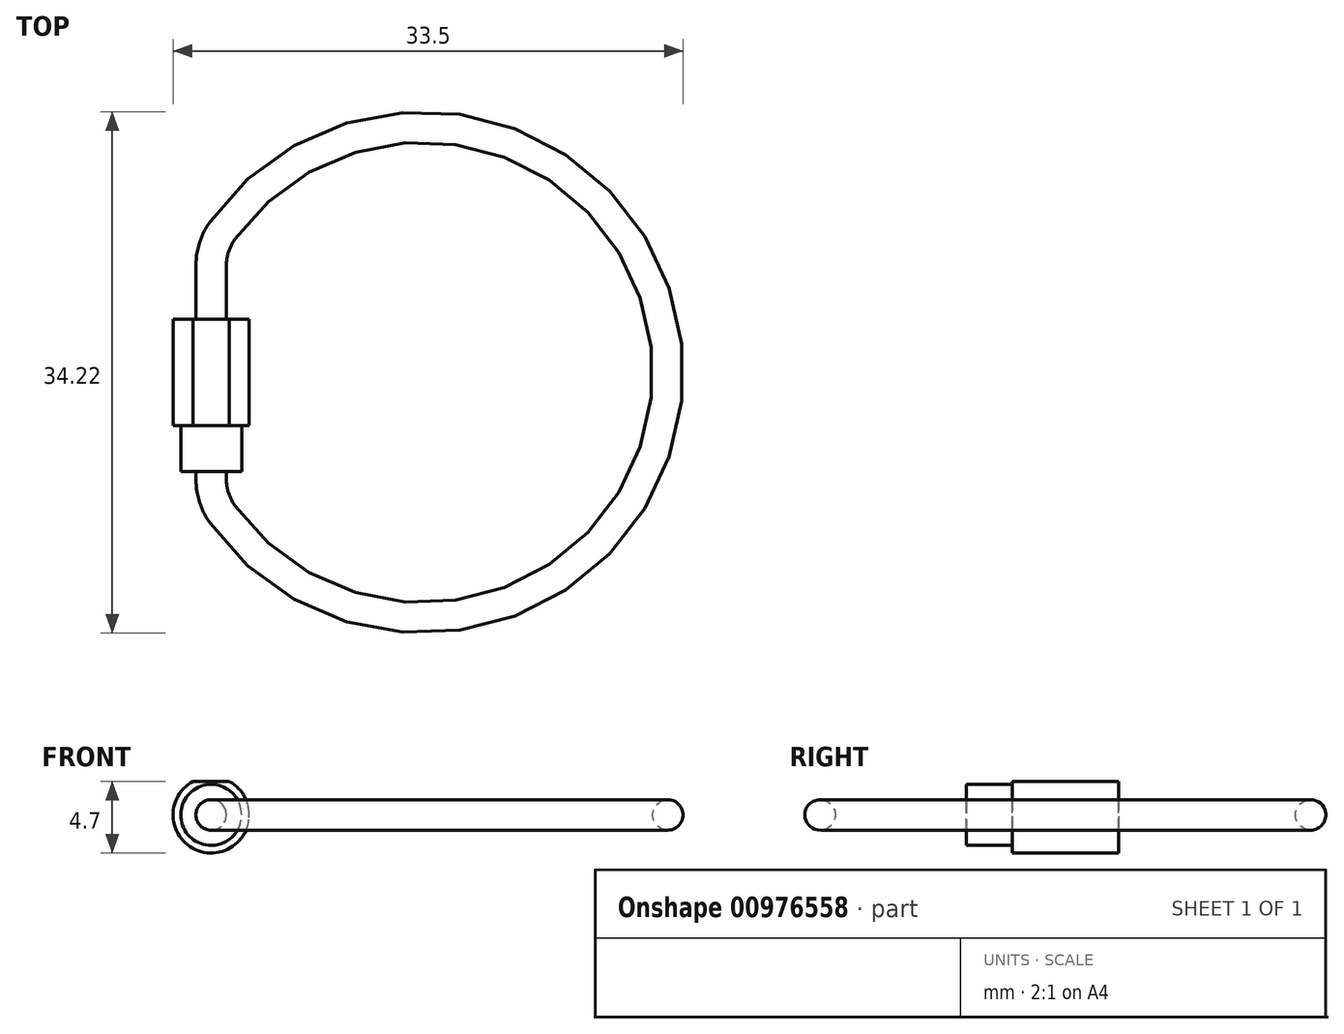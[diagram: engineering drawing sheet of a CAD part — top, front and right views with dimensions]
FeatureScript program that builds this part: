
annotation { "Feature Type Name" : "Feature", "Feature Type Description" : "" }
export const myFeature = defineFeature(function(context is Context, id is Id, definition is map)
    precondition{}
    {
        {
            var Q0;
            Q0=qCreatedBy(makeId("Front.planeOp"),FACE);
            var sketch = newSketch(context, id + "F0", { "sketchPlane" : qUnion([Q0])});
            skCircle(sketch, "E0", {"center": v(0, 0) * mm, "radius": 2.5 * mm});
            skSolve(sketch);
        }
        {
            var Q0;
            Q0=makeQuery(id+"F0.imprint","IMPRINT",FACE,{"disambiguationData":[TD([[makeQuery(id+"F0.imprint","IMPRINT",EDGE,{"derivedFrom":sQuery(id+"F0.wireOp",EDGE,"E0")}),1.0]])]});
            extrude(context, id + "F1", {"entities" : qUnion([Q0]), "endBound" : BoundingType.SYMMETRIC, "depth" : 7 * mm, "offsetDistance" : 25 * mm});
        }
        {
            var Q0;
            Q0=makeQuery(id+"F1.opExtrude","CAP_FACE",FACE,{"disambiguationData":[OSD([sQuery(id+"F0.wireOp",EDGE,"E0")])],"isStart":false});
            var sketch = newSketch(context, id + "F2", { "sketchPlane" : qUnion([Q0])});
            skLineSegment(sketch, "E1.bottom", {"start": v(-1.19, 2.5) * mm, "end": v(1.19, 2.5) * mm});
            skLineSegment(sketch, "E1.top", {"start": v(-1.19, 2.2) * mm, "end": v(1.19, 2.2) * mm});
            skLineSegment(sketch, "E1.left", {"start": v(-1.19, 2.5) * mm, "end": v(-1.19, 2.2) * mm});
            skLineSegment(sketch, "E1.right", {"start": v(1.19, 2.5) * mm, "end": v(1.19, 2.2) * mm});
            skSolve(sketch);
        }
        {
            var Q0;
            Q0 = qSketchRegion(id + "F2", true);
            extrude(context, id + "F3", {"entities" : qUnion([Q0]), "operationType" : NewBodyOperationType.REMOVE, "endBound" : BoundingType.THROUGH_ALL, "oppositeDirection" : true, "depth" : 25 * mm, "offsetDistance" : 25 * mm});
        }
        {
            var Q0;
            Q0=makeQuery(id+"F1.opExtrude","CAP_FACE",FACE,{"disambiguationData":[OSD([sQuery(id+"F0.wireOp",EDGE,"E0")])],"isStart":false});
            var sketch = newSketch(context, id + "F4", { "sketchPlane" : qUnion([Q0])});
            skCircle(sketch, "E2", {"center": v(0, 0) * mm, "radius": 2 * mm});
            skSolve(sketch);
        }
        {
            var Q0;
            Q0=makeQuery(id+"F4.imprint","IMPRINT",FACE,{"disambiguationData":[TD([[makeQuery(id+"F4.imprint","IMPRINT",EDGE,{"derivedFrom":sQuery(id+"F4.wireOp",EDGE,"E2")}),1.0]])]});
            extrude(context, id + "F5", {"entities" : qUnion([Q0]), "operationType" : NewBodyOperationType.ADD, "depth" : 3 * mm, "offsetDistance" : 25 * mm});
        }
        {
            var Q0;
            Q0=qCreatedBy(makeId("Top.planeOp"),FACE);
            var sketch = newSketch(context, id + "F6", { "sketchPlane" : qUnion([Q0])});
            skLineSegment(sketch, "E3", {"start": v(0, 0) * mm, "end": v(13.89, 0) * mm, "construction": true});
            skLineSegment(sketch, "E4", {"start": v(0, 7) * mm, "end": v(0, -7) * mm});
            skArc(sketch, "E5", {"start": v(0.74, 9.31) * mm, "mid": v(0.19, 8.21) * mm, "end": v(0, 7) * mm});
            skArc(sketch, "E6", {"start": v(0, -7) * mm, "mid": v(0.19, -8.21) * mm, "end": v(0.74, -9.31) * mm});
            skArc(sketch, "E7", {"start": v(0.74, -9.31) * mm, "mid": v(30, 0) * mm, "end": v(0.74, 9.31) * mm});
            skSolve(sketch);
        }
        {
            var Q0;
            Q0=makeQuery(id+"F5.opExtrude","CAP_FACE",FACE,{"disambiguationData":[OSD([sQuery(id+"F4.wireOp",EDGE,"E2")])],"isStart":false});
            var sketch = newSketch(context, id + "F7", { "sketchPlane" : qUnion([Q0])});
            skCircle(sketch, "E8", {"center": v(0, 0) * mm, "radius": 1 * mm});
            skSolve(sketch);
        }
        {
            var Q0;
            Q0=makeQuery(id+"F7.imprint","IMPRINT",FACE,{"disambiguationData":[TD([[makeQuery(id+"F7.imprint","IMPRINT",EDGE,{"derivedFrom":sQuery(id+"F7.wireOp",EDGE,"E8")}),1.0]])]});
            var Q1;
            Q1=sQuery(id+"F6.wireOp",EDGE,"E4");
            var Q2;
            Q2=sQuery(id+"F6.wireOp",EDGE,"E5");
            var Q3;
            Q3=sQuery(id+"F6.wireOp",EDGE,"E7");
            var Q4;
            Q4=sQuery(id+"F6.wireOp",EDGE,"E6");
            sweep(context, id + "F8", {"operationType" : NewBodyOperationType.ADD, "profiles" : qUnion([Q0]), "path" : qUnion([Q1, Q2, Q3, Q4])});
        }
    });
